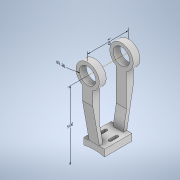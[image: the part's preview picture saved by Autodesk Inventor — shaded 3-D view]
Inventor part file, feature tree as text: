
AUTODESK INVENTOR PART (.ipt)
format: ipt  version: 2020.3 (Build 243373000, 373)  size: 220,672 bytes
history: native  units: in
note: dims shown in document units (in); Inventor stores cm internally (conversion verified against a paired STEP export)
features: extrude x6, sketch x6, other x5, plane x3, mirror x2
ambient origin geometry x8: Origin, YZ Plane, XZ Plane, XY Plane, X Axis, Y Axis, Z Axis, Center Point
bodies: Solid1 (feature_tree)
feature tree (22):
  other  "Annotations"
  extrude  "Extrusion1"  Depth=0.75in
  extrude  "Extrusion2"  Depth=2.0in TaperAngle=0.0deg
  mirror  "Mirror1"
  extrude  "Extrusion3"  Depth=0.4in
  plane  "Work Plane1"
  extrude  "Extrusion4"  TaperAngle=0.0deg  [1 undecoded]
  extrude  "Extrusion5"  Depth=0.2in
  mirror  "Mirror4"
  extrude  "Extrusion6"  Depth=0.25in
  plane  "Work Plane3"
  other  "Work Axis1"
  plane  "Work Plane4"
  sketch  "Sketch1"  dims[d1=6.0in d2=0.75in]
  sketch  "Sketch2"  dims[d3=0.5in d4=2.0in d5=0.0in]
  sketch  "Sketch3"  dims[d6=0.0in d7=0.4in]
  sketch  "Sketch4"  dims[d8=0.25in d9=0.0in d10=0.0in]
  sketch  "Sketch7"  dims[d11=0.2in d13=2.75in]
  sketch  "Sketch8"  dims[d14=0.0687in d15=0.25in d16=0.75in d17=0.0in d18=2.0in d19=1.2in d20=0.25in d21=0.5in d22=0.0in d25=1.75in d26=0.75in d27=0.0in d31=0.75in d32=0.0in d62=0.0039in d64=60.0deg d101=0.3779in d119=0.3779in d137=0.3779in d155=0.3779in d173=0.3779in d191=0.3779in d33=-0.1818in d34=5.0in d35=2.9698in d36=1.1814in d37=1.2in d28=0.5in d29=0.0344in]
  other  "Linear Dimension 1"
  other  "Linear Dimension 2"
  other  "Diameter Dimension 1"
note: 1 required parameter value undecoded (feature->parameter linkage not recoverable at this tier; creation-order binding heuristic only, values carry confidence <= 0.55)
